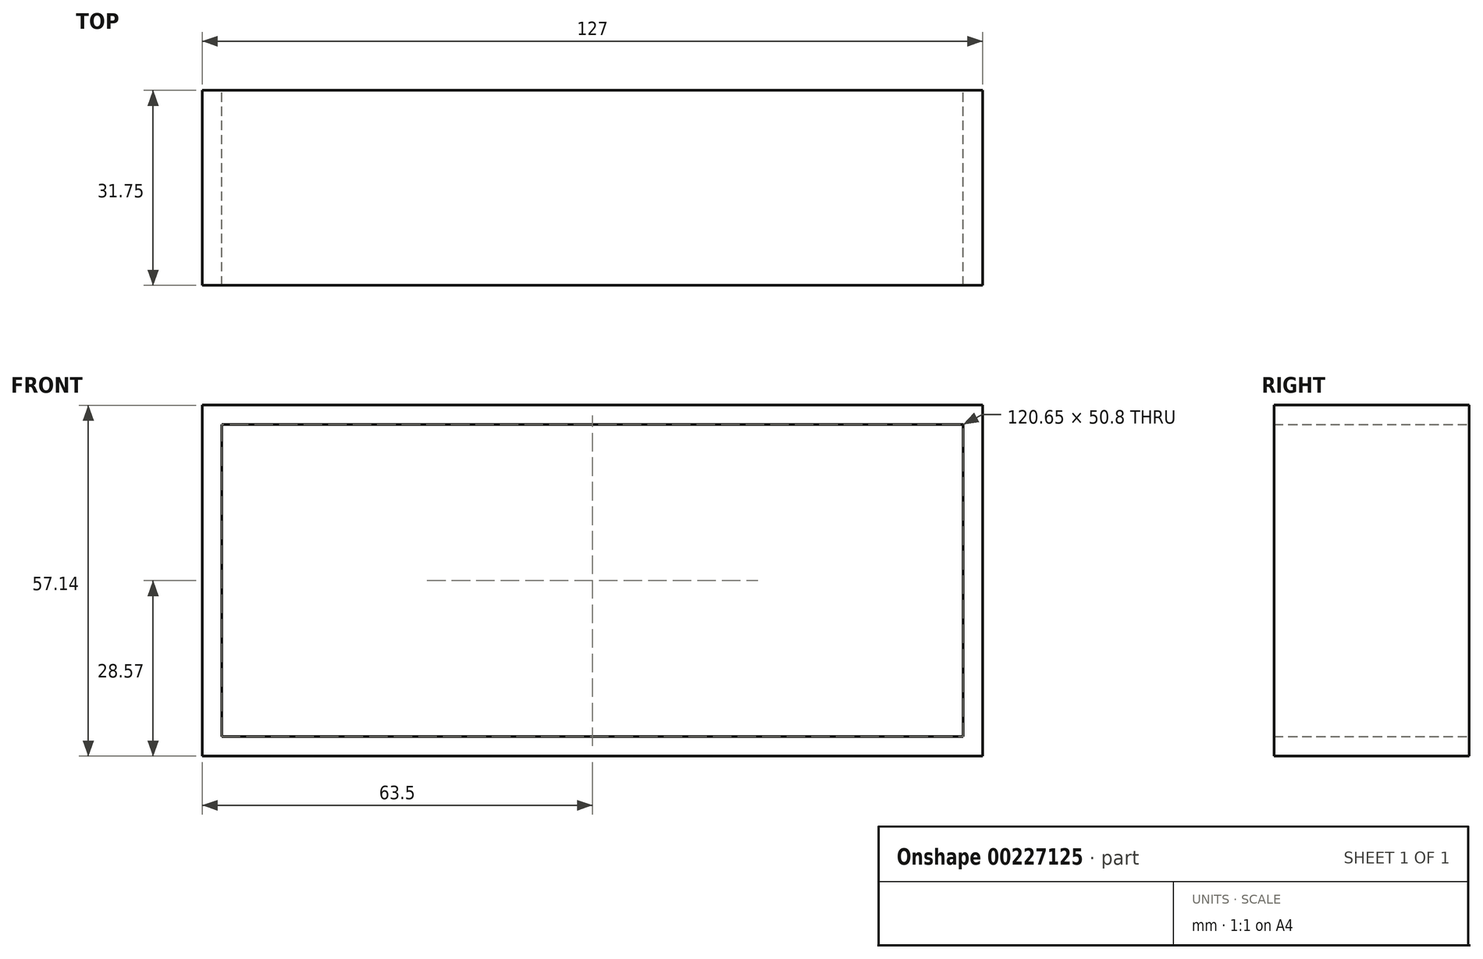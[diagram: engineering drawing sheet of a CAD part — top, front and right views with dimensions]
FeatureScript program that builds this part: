
annotation { "Feature Type Name" : "Feature", "Feature Type Description" : "" }
export const myFeature = defineFeature(function(context is Context, id is Id, definition is map)
    precondition{}
    {
        {
            var Q0;
            Q0=qCreatedBy(makeId("Front.planeOp"),FACE);
            var sketch = newSketch(context, id + "F0", { "sketchPlane" : qUnion([Q0])});
            skLineSegment(sketch, "E0.bottom", {"start": v(60.33, 25.4) * mm, "end": v(-60.33, 25.4) * mm});
            skLineSegment(sketch, "E0.top", {"start": v(60.33, -25.4) * mm, "end": v(-60.33, -25.4) * mm});
            skLineSegment(sketch, "E0.left", {"start": v(60.33, 25.4) * mm, "end": v(60.33, -25.4) * mm});
            skLineSegment(sketch, "E0.right", {"start": v(-60.33, 25.4) * mm, "end": v(-60.33, -25.4) * mm});
            skPoint(sketch, "E0.middle", {"position": v(0, 0) * mm});
            skLineSegment(sketch, "E1.bottom", {"start": v(63.5, 28.57) * mm, "end": v(-63.5, 28.57) * mm});
            skLineSegment(sketch, "E1.top", {"start": v(63.5, -28.57) * mm, "end": v(-63.5, -28.57) * mm});
            skLineSegment(sketch, "E1.left", {"start": v(63.5, 28.58) * mm, "end": v(63.5, -28.57) * mm});
            skLineSegment(sketch, "E1.right", {"start": v(-63.5, 28.58) * mm, "end": v(-63.5, -28.57) * mm});
            skSolve(sketch);
        }
        {
            var Q0;
            Q0=makeQuery(id+"F0.imprint","IMPRINT",FACE,{"disambiguationData":[TD([[makeQuery(id+"F0.imprint","IMPRINT",EDGE,{"derivedFrom":sQuery(id+"F0.wireOp",EDGE,"E0.bottom")}),-1.0]])]});
            extrude(context, id + "F1", {"entities" : qUnion([Q0]), "depth" : 31.75 * mm, "offsetDistance" : 25.4 * mm});
        }
    });
